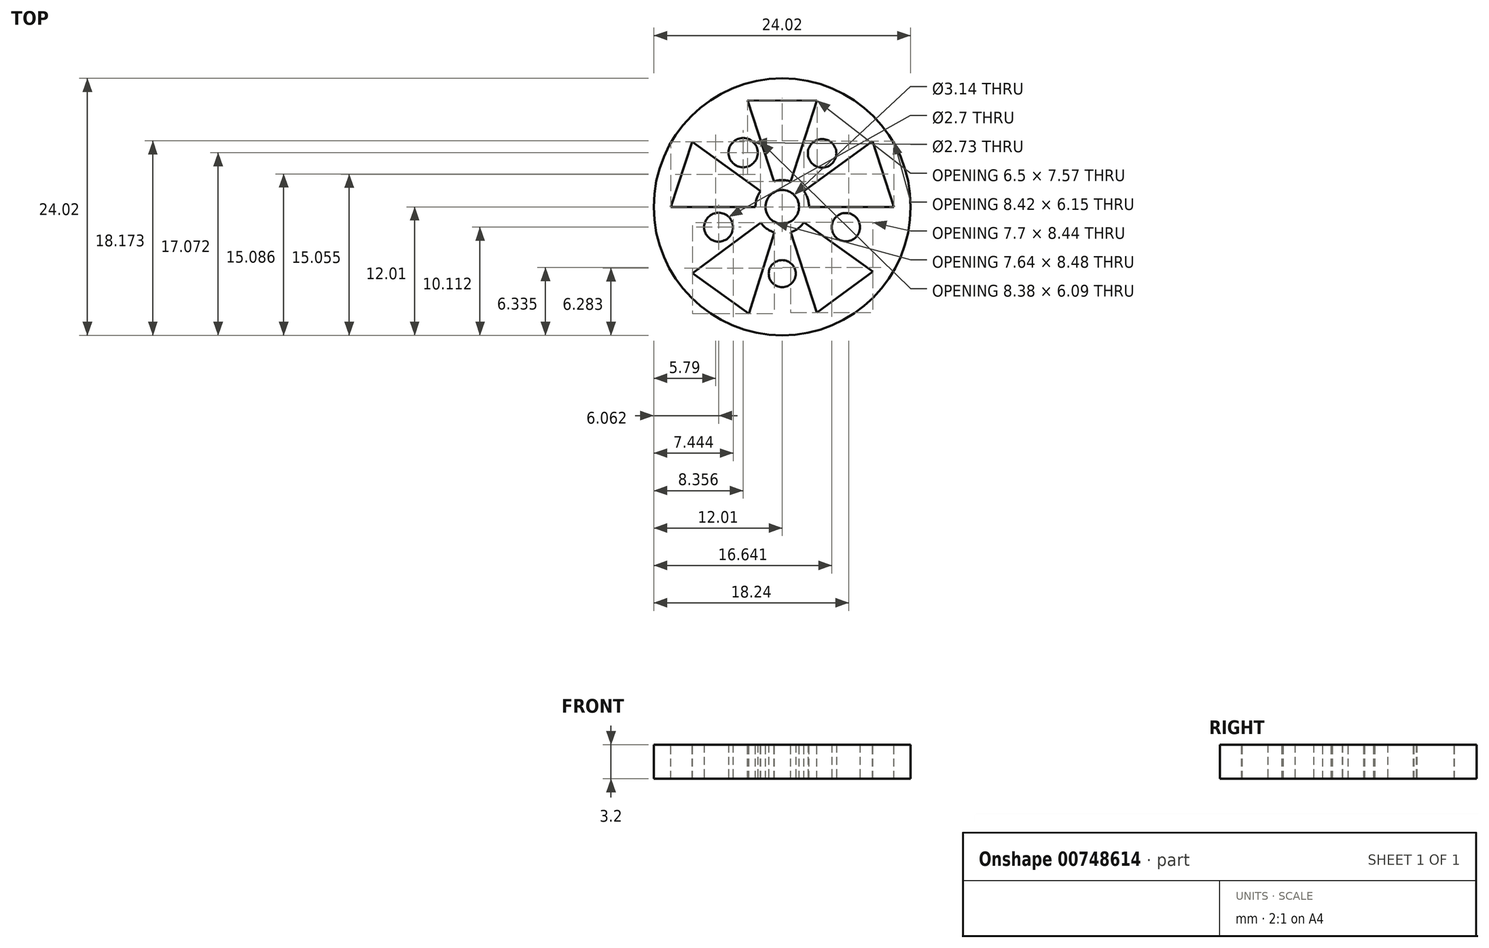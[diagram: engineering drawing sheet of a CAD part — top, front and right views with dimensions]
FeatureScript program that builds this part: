
annotation { "Feature Type Name" : "Feature", "Feature Type Description" : "" }
export const myFeature = defineFeature(function(context is Context, id is Id, definition is map)
    precondition{}
    {
        {
            var Q0;
            Q0=qCreatedBy(makeId("Top.planeOp"),FACE);
            var sketch = newSketch(context, id + "F0", { "sketchPlane" : qUnion([Q0])});
            skCircle(sketch, "E0", {"center": v(0, 0) * mm, "radius": 12.01 * mm});
            skSolve(sketch);
        }
        {
            var Q0;
            Q0=makeQuery(id+"F0.imprint","IMPRINT",FACE,{"disambiguationData":[TD([[makeQuery(id+"F0.imprint","IMPRINT",EDGE,{"derivedFrom":sQuery(id+"F0.wireOp",EDGE,"E0")}),1.0]])]});
            extrude(context, id + "F1", {"entities" : qUnion([Q0]), "depth" : 3.2 * mm, "offsetDistance" : 25 * mm});
        }
        {
            var Q0;
            Q0=makeQuery(id+"F1.opExtrude","CAP_FACE",FACE,{"disambiguationData":[OSD([sQuery(id+"F0.wireOp",EDGE,"E0")])],"isStart":false});
            var sketch = newSketch(context, id + "F2", { "sketchPlane" : qUnion([Q0])});
            skCircle(sketch, "E1", {"center": v(0, 0) * mm, "radius": 1.57 * mm});
            skSolve(sketch);
        }
        {
            var Q0;
            Q0 = qSketchRegion(id + "F2", true);
            extrude(context, id + "F3", {"entities" : qUnion([Q0]), "operationType" : NewBodyOperationType.REMOVE, "oppositeDirection" : true, "depth" : 25 * mm, "offsetDistance" : 25 * mm});
        }
        {
            var Q0;
            Q0=makeQuery(id+"F1.opExtrude","CAP_FACE",FACE,{"disambiguationData":[OSD([sQuery(id+"F0.wireOp",EDGE,"E0")])],"isStart":false});
            var sketch = newSketch(context, id + "F4", { "sketchPlane" : qUnion([Q0])});
            skCircle(sketch, "E2", {"center": v(0, 0) * mm, "radius": 2.5 * mm});
            skSolve(sketch);
        }
        {
            var Q0;
            Q0=makeQuery(id+"F4.imprint","IMPRINT",FACE,{"disambiguationData":[TD([[makeQuery(id+"F4.imprint","IMPRINT",EDGE,{"derivedFrom":sQuery(id+"F4.wireOp",EDGE,"E2")}),-1.0]])]});
            var sketch = newSketch(context, id + "F5", { "sketchPlane" : qUnion([Q0])});
            skCircle(sketch, "E3.cCircle", {"center": v(0, 0) * mm, "radius": 9.89 * mm, "construction": true});
            skLineSegment(sketch, "E3.0", {"start": v(-3.21, 9.89) * mm, "end": v(3.21, 9.89) * mm});
            skLineSegment(sketch, "E3.1", {"start": v(3.21, 9.89) * mm, "end": v(8.41, 6.11) * mm});
            skLineSegment(sketch, "E3.2", {"start": v(8.41, 6.11) * mm, "end": v(10.4, 0) * mm});
            skLineSegment(sketch, "E3.3", {"start": v(10.4, 0) * mm, "end": v(8.41, -6.11) * mm});
            skLineSegment(sketch, "E3.4", {"start": v(8.41, -6.11) * mm, "end": v(3.21, -9.89) * mm});
            skLineSegment(sketch, "E3.5", {"start": v(3.21, -9.89) * mm, "end": v(-3.21, -9.89) * mm});
            skLineSegment(sketch, "E3.6", {"start": v(-3.21, -9.89) * mm, "end": v(-8.41, -6.11) * mm});
            skLineSegment(sketch, "E3.7", {"start": v(-8.41, -6.11) * mm, "end": v(-10.4, 0) * mm});
            skLineSegment(sketch, "E3.8", {"start": v(-10.4, 0) * mm, "end": v(-8.41, 6.11) * mm});
            skLineSegment(sketch, "E3.9", {"start": v(-8.41, 6.11) * mm, "end": v(-3.21, 9.89) * mm});
            skPoint(sketch, "E3.0.midPoint", {"position": v(0, 9.89) * mm});
            skSolve(sketch);
        }
        {
            var Q0;
            Q0=makeQuery(id+"F4.imprint","IMPRINT",FACE,{"disambiguationData":[TD([[makeQuery(id+"F4.imprint","IMPRINT",EDGE,{"derivedFrom":sQuery(id+"F4.wireOp",EDGE,"E2")}),-1.0]])]});
            var sketch = newSketch(context, id + "F6", { "sketchPlane" : qUnion([Q0])});
            skLineSegment(sketch, "E4", {"start": v(0, 0) * mm, "end": v(-3.12, -9.97) * mm});
            skLineSegment(sketch, "E5", {"start": v(0, 0) * mm, "end": v(3.25, -9.9) * mm});
            skLineSegment(sketch, "E6", {"start": v(8.48, -6.05) * mm, "end": v(0, 0) * mm});
            skLineSegment(sketch, "E7", {"start": v(10.44, 0) * mm, "end": v(0, 0) * mm});
            skLineSegment(sketch, "E8", {"start": v(0, 0) * mm, "end": v(-10.41, 0) * mm});
            skLineSegment(sketch, "E9", {"start": v(-8.38, -6.2) * mm, "end": v(0, 0) * mm});
            skLineSegment(sketch, "E10", {"start": v(8.45, 6.15) * mm, "end": v(0, 0) * mm});
            skLineSegment(sketch, "E11", {"start": v(3.25, 9.92) * mm, "end": v(0, 0) * mm});
            skLineSegment(sketch, "E12", {"start": v(-3.25, 9.95) * mm, "end": v(0, 0) * mm});
            skLineSegment(sketch, "E13", {"start": v(-8.43, 6.09) * mm, "end": v(0, 0) * mm});
            skLineSegment(sketch, "E14", {"start": v(3.25, -9.9) * mm, "end": v(8.48, -6.05) * mm});
            skLineSegment(sketch, "E15", {"start": v(8.48, -6.05) * mm, "end": v(10.44, 0) * mm});
            skLineSegment(sketch, "E16", {"start": v(10.44, 0) * mm, "end": v(8.45, 6.15) * mm});
            skLineSegment(sketch, "E17", {"start": v(8.45, 6.15) * mm, "end": v(3.25, 9.92) * mm});
            skLineSegment(sketch, "E18", {"start": v(3.25, 9.92) * mm, "end": v(-3.25, 9.95) * mm});
            skLineSegment(sketch, "E19", {"start": v(-3.25, 9.95) * mm, "end": v(-8.43, 6.09) * mm});
            skLineSegment(sketch, "E20", {"start": v(-8.43, 6.09) * mm, "end": v(-10.41, 0) * mm});
            skLineSegment(sketch, "E21", {"start": v(-10.41, 0) * mm, "end": v(-8.38, -6.2) * mm});
            skLineSegment(sketch, "E22", {"start": v(-3.12, -9.97) * mm, "end": v(-8.38, -6.2) * mm});
            skLineSegment(sketch, "E23", {"start": v(-3.12, -9.97) * mm, "end": v(3.25, -9.9) * mm});
            skSolve(sketch);
        }
        {
            var Q0;
            Q0=makeQuery(id+"F4.imprint","IMPRINT",FACE,{"disambiguationData":[TD([[makeQuery(id+"F4.imprint","IMPRINT",EDGE,{"derivedFrom":sQuery(id+"F4.wireOp",EDGE,"E2")}),-1.0]])]});
            var sketch = newSketch(context, id + "F7", { "sketchPlane" : qUnion([Q0])});
            skSolve(sketch);
        }
        {
            var Q0;
            {var subQ0=sQuery(id+"F6.wireOp",EDGE,"E18");Q0=makeQuery(id+"F6.imprint","IMPRINT",FACE,{"disambiguationData":[TD([[makeQuery(id+"F6.imprint","IMPRINT",EDGE,{"derivedFrom":subQ0}),1.0]])]});}
            var Q1;
            {var subQ0=sQuery(id+"F6.wireOp",EDGE,"E16");Q1=makeQuery(id+"F6.imprint","IMPRINT",FACE,{"disambiguationData":[TD([[makeQuery(id+"F6.imprint","IMPRINT",EDGE,{"derivedFrom":subQ0}),1.0]])]});}
            var Q2;
            {var subQ0=sQuery(id+"F6.wireOp",EDGE,"E14");Q2=makeQuery(id+"F6.imprint","IMPRINT",FACE,{"disambiguationData":[TD([[makeQuery(id+"F6.imprint","IMPRINT",EDGE,{"derivedFrom":subQ0}),1.0]])]});}
            var Q3;
            {var subQ0=sQuery(id+"F6.wireOp",EDGE,"E22");Q3=makeQuery(id+"F6.imprint","IMPRINT",FACE,{"disambiguationData":[TD([[makeQuery(id+"F6.imprint","IMPRINT",EDGE,{"derivedFrom":subQ0}),-1.0]])]});}
            var Q4;
            {var subQ0=sQuery(id+"F6.wireOp",EDGE,"E20");Q4=makeQuery(id+"F6.imprint","IMPRINT",FACE,{"disambiguationData":[TD([[makeQuery(id+"F6.imprint","IMPRINT",EDGE,{"derivedFrom":subQ0}),1.0]])]});}
            var Q5;
            Q5=sQuery(id+"F6.wireOp",EDGE,"E11");
            var Q6;
            Q6=sQuery(id+"F6.wireOp",EDGE,"E12");
            var Q7;
            Q7=sQuery(id+"F5.wireOp",EDGE,"E3.0");
            extrude(context, id + "F8", {"entities" : qUnion([Q0, Q1, Q2, Q3, Q4]), "operationType" : NewBodyOperationType.REMOVE, "surfaceEntities" : qUnion([Q5, Q6, Q7]), "oppositeDirection" : true, "depth" : 25 * mm, "offsetDistance" : 25 * mm});
        }
        {
            var Q0;
            Q0=makeQuery(id+"FpxfZz38iCK11fa_1.imprint","IMPRINT",FACE,{"disambiguationData":[TD([[makeQuery(id+"FpxfZz38iCK11fa_1.imprint","IMPRINT",EDGE,{"derivedFrom":sQuery(id+"FpxfZz38iCK11fa_1.wireOp",EDGE,"FryadZUQ-JLp6-2EG7-rDIz-w7h9wu3mHMRW")}),-1.0]])]});
            var sketch = newSketch(context, id + "F9", { "sketchPlane" : qUnion([Q0])});
            skSolve(sketch);
        }
        {
            var Q0;
            Q0=makeQuery(id+"F1.opExtrude","CAP_FACE",FACE,{"disambiguationData":[OSD([sQuery(id+"F0.wireOp",EDGE,"E0")])],"isStart":true});
            var sketch = newSketch(context, id + "F10", { "sketchPlane" : qUnion([Q0])});
            skCircle(sketch, "E24", {"center": v(0, 0) * mm, "radius": 6.24 * mm});
            skCircle(sketch, "E25", {"center": v(-3.65, -5.06) * mm, "radius": 1.36 * mm});
            skCircle(sketch, "E26", {"center": v(-5.95, 1.9) * mm, "radius": 1.35 * mm});
            skCircle(sketch, "E27", {"center": v(0, 6.24) * mm, "radius": 1.26 * mm});
            skCircle(sketch, "E28", {"center": v(5.95, 1.9) * mm, "radius": 1.33 * mm});
            skCircle(sketch, "E29", {"center": v(3.73, -5) * mm, "radius": 1.33 * mm});
            skSolve(sketch);
        }
        {
            var Q0;
            {var subQ0=sQuery(id+"F10.wireOp",EDGE,"E26");var subQ1=sQuery(id+"F10.wireOp",EDGE,"E24");var subQ2=makeQuery(id+"F10.imprint","INTERSECT",VERTEX,{"disambiguationData":[OD(0.0)],"derivedFrom":[subQ1,subQ0]});Q0=makeQuery(id+"F10.imprint","IMPRINT",FACE,{"disambiguationData":[TD([[makeQuery(id+"F10.imprint","IMPRINT",EDGE,{"disambiguationData":[TD([[subQ2,-1.0]])],"derivedFrom":subQ1}),-1.0]])]});}
            var Q1;
            {var subQ0=sQuery(id+"F10.wireOp",EDGE,"E26");var subQ1=sQuery(id+"F10.wireOp",EDGE,"E24");var subQ2=makeQuery(id+"F10.imprint","INTERSECT",VERTEX,{"disambiguationData":[OD(0.0)],"derivedFrom":[subQ1,subQ0]});Q1=makeQuery(id+"F10.imprint","IMPRINT",FACE,{"disambiguationData":[TD([[makeQuery(id+"F10.imprint","IMPRINT",EDGE,{"disambiguationData":[TD([[subQ2,-1.0]])],"derivedFrom":subQ1}),1.0]])]});}
            var Q2;
            {var subQ0=sQuery(id+"F10.wireOp",EDGE,"E27");var subQ1=sQuery(id+"F10.wireOp",EDGE,"E24");var subQ2=makeQuery(id+"F10.imprint","INTERSECT",VERTEX,{"disambiguationData":[OD(0.0)],"derivedFrom":[subQ1,subQ0]});Q2=makeQuery(id+"F10.imprint","IMPRINT",FACE,{"disambiguationData":[TD([[makeQuery(id+"F10.imprint","IMPRINT",EDGE,{"disambiguationData":[TD([[subQ2,-1.0]])],"derivedFrom":subQ1}),-1.0]])]});}
            var Q3;
            {var subQ0=sQuery(id+"F10.wireOp",EDGE,"E27");var subQ1=sQuery(id+"F10.wireOp",EDGE,"E24");var subQ2=makeQuery(id+"F10.imprint","INTERSECT",VERTEX,{"disambiguationData":[OD(0.0)],"derivedFrom":[subQ1,subQ0]});Q3=makeQuery(id+"F10.imprint","IMPRINT",FACE,{"disambiguationData":[TD([[makeQuery(id+"F10.imprint","IMPRINT",EDGE,{"disambiguationData":[TD([[subQ2,-1.0]])],"derivedFrom":subQ1}),1.0]])]});}
            var Q4;
            {var subQ0=sQuery(id+"F10.wireOp",EDGE,"E28");var subQ1=sQuery(id+"F10.wireOp",EDGE,"E24");var subQ2=makeQuery(id+"F10.imprint","INTERSECT",VERTEX,{"disambiguationData":[OD(0.0)],"derivedFrom":[subQ1,subQ0]});Q4=makeQuery(id+"F10.imprint","IMPRINT",FACE,{"disambiguationData":[TD([[makeQuery(id+"F10.imprint","IMPRINT",EDGE,{"disambiguationData":[TD([[subQ2,-1.0]])],"derivedFrom":subQ1}),1.0]])]});}
            var Q5;
            {var subQ0=sQuery(id+"F10.wireOp",EDGE,"E28");var subQ1=sQuery(id+"F10.wireOp",EDGE,"E24");var subQ2=makeQuery(id+"F10.imprint","INTERSECT",VERTEX,{"disambiguationData":[OD(0.0)],"derivedFrom":[subQ1,subQ0]});Q5=makeQuery(id+"F10.imprint","IMPRINT",FACE,{"disambiguationData":[TD([[makeQuery(id+"F10.imprint","IMPRINT",EDGE,{"disambiguationData":[TD([[subQ2,-1.0]])],"derivedFrom":subQ1}),-1.0]])]});}
            var Q6;
            {var subQ0=sQuery(id+"F10.wireOp",EDGE,"E29");var subQ1=sQuery(id+"F10.wireOp",EDGE,"E24");var subQ2=makeQuery(id+"F10.imprint","INTERSECT",VERTEX,{"disambiguationData":[OD(0.0)],"derivedFrom":[subQ1,subQ0]});Q6=makeQuery(id+"F10.imprint","IMPRINT",FACE,{"disambiguationData":[TD([[makeQuery(id+"F10.imprint","IMPRINT",EDGE,{"disambiguationData":[TD([[subQ2,-1.0]])],"derivedFrom":subQ1}),-1.0]])]});}
            var Q7;
            {var subQ0=sQuery(id+"F10.wireOp",EDGE,"E29");var subQ1=sQuery(id+"F10.wireOp",EDGE,"E24");var subQ2=makeQuery(id+"F10.imprint","INTERSECT",VERTEX,{"disambiguationData":[OD(0.0)],"derivedFrom":[subQ1,subQ0]});Q7=makeQuery(id+"F10.imprint","IMPRINT",FACE,{"disambiguationData":[TD([[makeQuery(id+"F10.imprint","IMPRINT",EDGE,{"disambiguationData":[TD([[subQ2,-1.0]])],"derivedFrom":subQ1}),1.0]])]});}
            var Q8;
            {var subQ0=sQuery(id+"F10.wireOp",EDGE,"E25");var subQ1=sQuery(id+"F10.wireOp",EDGE,"E24");var subQ2=makeQuery(id+"F10.imprint","INTERSECT",VERTEX,{"disambiguationData":[OD(0.0)],"derivedFrom":[subQ1,subQ0]});Q8=makeQuery(id+"F10.imprint","IMPRINT",FACE,{"disambiguationData":[TD([[makeQuery(id+"F10.imprint","IMPRINT",EDGE,{"disambiguationData":[TD([[subQ2,-1.0]])],"derivedFrom":subQ1}),1.0]])]});}
            var Q9;
            {var subQ0=sQuery(id+"F10.wireOp",EDGE,"E25");var subQ1=sQuery(id+"F10.wireOp",EDGE,"E24");var subQ2=makeQuery(id+"F10.imprint","INTERSECT",VERTEX,{"disambiguationData":[OD(0.0)],"derivedFrom":[subQ1,subQ0]});Q9=makeQuery(id+"F10.imprint","IMPRINT",FACE,{"disambiguationData":[TD([[makeQuery(id+"F10.imprint","IMPRINT",EDGE,{"disambiguationData":[TD([[subQ2,-1.0]])],"derivedFrom":subQ1}),-1.0]])]});}
            extrude(context, id + "F11", {"entities" : qUnion([Q0, Q1, Q2, Q3, Q4, Q5, Q6, Q7, Q8, Q9]), "operationType" : NewBodyOperationType.REMOVE, "oppositeDirection" : true, "depth" : 25 * mm, "offsetDistance" : 25 * mm});
        }
    });
